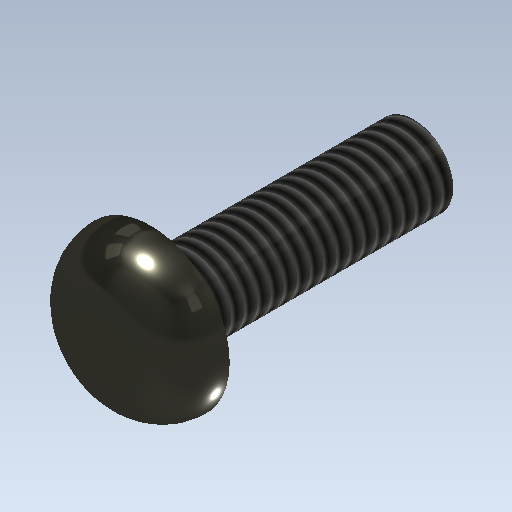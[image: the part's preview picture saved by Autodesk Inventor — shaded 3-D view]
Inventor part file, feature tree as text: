
AUTODESK INVENTOR PART (.ipt)
format: ipt  version: 2020.2 (Build 242310000, 310)  size: 186,368 bytes
history: native  units: mm
features: extrude x4, sketch x4, other x1, fillet x1, thread x1
ambient origin geometry x1: Origin
bodies: Body1 (feature_tree)
feature tree (11):
  other  "ソリッド1"
  extrude  "押し出し1"  Depth=3.0mm
  extrude  "押し出し2"  Depth=6.0mm TaperAngle=0.0deg
  fillet  "フィレット1"  Radius=6.0mm
  thread  "ねじ1"
  extrude  "押し出し3"  Depth=2.0mm TaperAngle=0.0deg
  extrude  "押し出し4"  Depth=2.0mm
  sketch  "スケッチ1"
  sketch  "スケッチ2"
  sketch  "スケッチ3"
  sketch  "スケッチ4"
